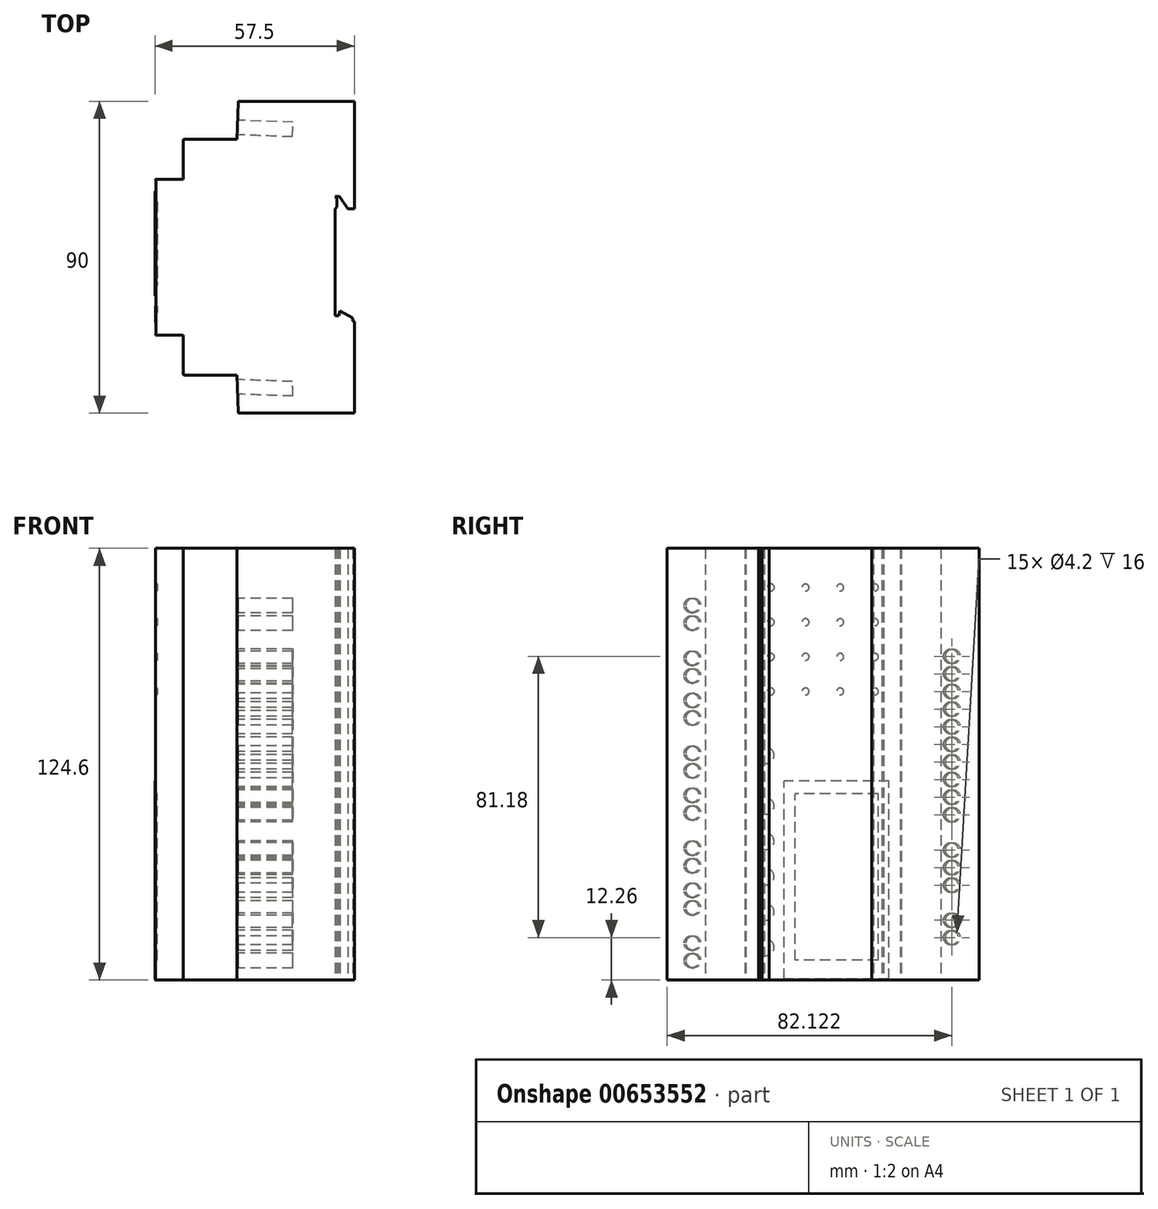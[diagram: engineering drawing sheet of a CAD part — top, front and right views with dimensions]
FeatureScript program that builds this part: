
annotation { "Feature Type Name" : "Feature", "Feature Type Description" : "" }
export const myFeature = defineFeature(function(context is Context, id is Id, definition is map)
    precondition{}
    {
        {
            var Q0;
            Q0=qCreatedBy(makeId("Top.planeOp"),FACE);
            var sketch = newSketch(context, id + "F0", { "sketchPlane" : qUnion([Q0])});
            skLineSegment(sketch, "E0", {"start": v(-15.51, -38) * mm, "end": v(4.7, -38) * mm});
            skLineSegment(sketch, "E1", {"start": v(17.7, -38) * mm, "end": v(17.7, -11.6) * mm});
            skLineSegment(sketch, "E2", {"start": v(5.2, -38) * mm, "end": v(17.7, -38) * mm});
            skLineSegment(sketch, "E3", {"start": v(17.2, -10.59) * mm, "end": v(13.57, -8.5) * mm});
            skLineSegment(sketch, "E4", {"start": v(17.2, -10.59) * mm, "end": v(17.2, -11.46) * mm});
            skLineSegment(sketch, "E5", {"start": v(13.57, -8.5) * mm, "end": v(13.2, -9.9) * mm});
            skLineSegment(sketch, "E6", {"start": v(-31.7, -15.5) * mm, "end": v(-39.4, -15.5) * mm});
            skLineSegment(sketch, "E7", {"start": v(-31.4, -27) * mm, "end": v(-16.19, -27) * mm});
            skLineSegment(sketch, "E8", {"start": v(-16.19, -27) * mm, "end": v(-15.81, -37.7) * mm});
            skArc(sketch, "E9", {"start": v(-15.81, -37.7) * mm, "mid": v(-15.72, -37.9) * mm, "end": v(-15.51, -38) * mm});
            skLineSegment(sketch, "E10", {"start": v(-31.7, -26.7) * mm, "end": v(-31.7, -15.5) * mm});
            skArc(sketch, "E11", {"start": v(-31.7, -26.7) * mm, "mid": v(-31.61, -26.9) * mm, "end": v(-31.4, -27) * mm});
            skLineSegment(sketch, "E12", {"start": v(17.7, 52) * mm, "end": v(-15.51, 52) * mm});
            skLineSegment(sketch, "E13", {"start": v(17.7, 52) * mm, "end": v(17.7, 21) * mm});
            skLineSegment(sketch, "E14", {"start": v(13.4, 24.5) * mm, "end": v(15.85, 21) * mm});
            skLineSegment(sketch, "E15", {"start": v(15.85, 21) * mm, "end": v(17.7, 21) * mm});
            skLineSegment(sketch, "E16", {"start": v(12.7, 24) * mm, "end": v(12.7, 21.5) * mm});
            skLineSegment(sketch, "E17", {"start": v(12.7, 21.5) * mm, "end": v(12.2, 21) * mm});
            skLineSegment(sketch, "E18", {"start": v(12.7, 24) * mm, "end": v(12.2, 24.5) * mm});
            skLineSegment(sketch, "E19", {"start": v(-31.7, 29.5) * mm, "end": v(-39.4, 29.5) * mm});
            skLineSegment(sketch, "E20", {"start": v(-31.7, 29.5) * mm, "end": v(-31.7, 40.7) * mm});
            skLineSegment(sketch, "E21", {"start": v(-16.19, 41) * mm, "end": v(-31.4, 41) * mm});
            skLineSegment(sketch, "E22", {"start": v(-15.81, 51.72) * mm, "end": v(-16.19, 41) * mm});
            skArc(sketch, "E23", {"start": v(-15.51, 52) * mm, "mid": v(-15.72, 51.92) * mm, "end": v(-15.81, 51.72) * mm});
            skArc(sketch, "E24", {"start": v(-31.4, 41) * mm, "mid": v(-31.61, 40.92) * mm, "end": v(-31.7, 40.7) * mm});
            skLineSegment(sketch, "E25", {"start": v(13.2, -9.9) * mm, "end": v(12.2, -9.9) * mm});
            skLineSegment(sketch, "E26", {"start": v(4.7, -38) * mm, "end": v(5.2, -38) * mm});
            skLineSegment(sketch, "E27", {"start": v(13.4, 24.5) * mm, "end": v(12.2, 24.5) * mm});
            skLineSegment(sketch, "E28", {"start": v(12.2, -9.9) * mm, "end": v(12.2, 21) * mm});
            skLineSegment(sketch, "E29", {"start": v(17.2, -11.46) * mm, "end": v(17.7, -11.6) * mm});
            skLineSegment(sketch, "E30", {"start": v(-39.7, 29.2) * mm, "end": v(-39.7, -15.2) * mm});
            skLineSegment(sketch, "E31", {"start": v(-39.7, -15.2) * mm, "end": v(-39.7, -15.5) * mm});
            skLineSegment(sketch, "E32", {"start": v(-39.7, -15.5) * mm, "end": v(-39.4, -15.5) * mm});
            skLineSegment(sketch, "E33", {"start": v(-39.7, 29.2) * mm, "end": v(-39.7, 29.5) * mm});
            skLineSegment(sketch, "E34", {"start": v(-39.7, 29.5) * mm, "end": v(-39.4, 29.5) * mm});
            skSolve(sketch);
        }
        {
            var Q0;
            Q0=makeQuery(id+"F0.imprint","IMPRINT",FACE,{"disambiguationData":[TD([[makeQuery(id+"F0.imprint","IMPRINT",EDGE,{"derivedFrom":sQuery(id+"F0.wireOp",EDGE,"E0")}),1.0]])]});
            extrude(context, id + "F1", {"entities" : qUnion([Q0]), "depth" : 124.6 * mm, "offsetDistance" : 25 * mm});
        }
        {
            var Q0;
            Q0=makeQuery(id+"F1.opExtrude","SWEPT_EDGE",EDGE,{"disambiguationData":[OSD([sQuery(id+"F0.wireOp",EDGE,"E31"),sQuery(id+"F0.wireOp",EDGE,"E32")])]});
            var Q1;
            Q1=makeQuery(id+"F1.opExtrude","SWEPT_EDGE",EDGE,{"disambiguationData":[OSD([sQuery(id+"F0.wireOp",EDGE,"E33"),sQuery(id+"F0.wireOp",EDGE,"E34")])]});
            fillet(context, id + "F2", {"entities" : qUnion([Q0, Q1]), "radius" : 0.25 * mm, "tangentPropagation" : true, "allowEdgeOverflow" : false});
        }
        {
            var Q0;
            Q0=makeQuery(id+"F1.opExtrude","SWEPT_FACE",FACE,{"disambiguationData":[OSD([sQuery(id+"F0.wireOp",EDGE,"E22")])]});
            var sketch = newSketch(context, id + "F3", { "sketchPlane" : qUnion([Q0])});
            skCircle(sketch, "E35", {"center": v(-43.82, 12.26) * mm, "radius": 2.1 * mm});
            skCircle(sketch, "E36", {"center": v(-43.82, 17.26) * mm, "radius": 2.1 * mm});
            skCircle(sketch, "E37", {"center": v(-43.82, 27.4) * mm, "radius": 2.1 * mm});
            skCircle(sketch, "E38.0.1.0", {"center": v(-43.82, 32.48) * mm, "radius": 2.1 * mm});
            skCircle(sketch, "E38.0.2.0", {"center": v(-43.82, 37.56) * mm, "radius": 2.1 * mm});
            skCircle(sketch, "E38.0.3.0", {"center": v(-43.82, 42.64) * mm, "radius": 2.1 * mm});
            skCircle(sketch, "E38.0.4.0", {"center": v(-43.82, 47.72) * mm, "radius": 2.1 * mm});
            skCircle(sketch, "E38.0.5.0", {"center": v(-43.82, 52.8) * mm, "radius": 2.1 * mm});
            skCircle(sketch, "E38.0.6.0", {"center": v(-43.82, 57.88) * mm, "radius": 2.1 * mm});
            skCircle(sketch, "E38.0.7.0", {"center": v(-43.82, 62.96) * mm, "radius": 2.1 * mm});
            skCircle(sketch, "E38.0.8.0", {"center": v(-43.82, 68.04) * mm, "radius": 2.1 * mm});
            skCircle(sketch, "E38.0.9.0", {"center": v(-43.82, 73.12) * mm, "radius": 2.1 * mm});
            skCircle(sketch, "E38.0.10.0", {"center": v(-43.82, 78.2) * mm, "radius": 2.1 * mm});
            skCircle(sketch, "E38.0.11.0", {"center": v(-43.82, 83.28) * mm, "radius": 2.1 * mm});
            skCircle(sketch, "E38.0.12.0", {"center": v(-43.82, 88.36) * mm, "radius": 2.1 * mm});
            skCircle(sketch, "E38.0.13.0", {"center": v(-43.82, 93.44) * mm, "radius": 2.1 * mm});
            skLineSegment(sketch, "E38.direction1", {"start": v(-43.82, 27.4) * mm, "end": v(-18.82, 27.4) * mm, "construction": true});
            skLineSegment(sketch, "E38.direction2", {"start": v(-43.82, 27.4) * mm, "end": v(-43.82, 32.48) * mm, "construction": true});
            skSolve(sketch);
        }
        {
            var Q0;
            Q0=makeQuery(id+"F1.opExtrude","SWEPT_FACE",FACE,{"disambiguationData":[OSD([sQuery(id+"F0.wireOp",EDGE,"E8")])]});
            var sketch = newSketch(context, id + "F4", { "sketchPlane" : qUnion([Q0])});
            skCircle(sketch, "E39", {"center": v(29.83, 5.64) * mm, "radius": 2.1 * mm});
            skCircle(sketch, "E40", {"center": v(29.83, 10.68) * mm, "radius": 2.1 * mm});
            skCircle(sketch, "E41", {"center": v(29.83, 20.84) * mm, "radius": 2.1 * mm});
            skCircle(sketch, "E42", {"center": v(29.83, 25.92) * mm, "radius": 2.1 * mm});
            skCircle(sketch, "E43", {"center": v(29.83, 33) * mm, "radius": 2.1 * mm});
            skCircle(sketch, "E44", {"center": v(29.83, 38.08) * mm, "radius": 2.1 * mm});
            skCircle(sketch, "E45.0.1.0", {"center": v(29.83, 60.4) * mm, "radius": 2.1 * mm});
            skCircle(sketch, "E45.0.1.1", {"center": v(29.83, 65.48) * mm, "radius": 2.1 * mm});
            skCircle(sketch, "E45.0.1.2", {"center": v(29.83, 53.32) * mm, "radius": 2.1 * mm});
            skCircle(sketch, "E45.0.1.3", {"center": v(29.83, 48.24) * mm, "radius": 2.1 * mm});
            skCircle(sketch, "E45.0.2.0", {"center": v(29.83, 87.8) * mm, "radius": 2.1 * mm});
            skCircle(sketch, "E45.0.2.1", {"center": v(29.83, 92.88) * mm, "radius": 2.1 * mm});
            skCircle(sketch, "E45.0.2.2", {"center": v(29.83, 80.72) * mm, "radius": 2.1 * mm});
            skCircle(sketch, "E45.0.2.3", {"center": v(29.83, 75.64) * mm, "radius": 2.1 * mm});
            skLineSegment(sketch, "E45.direction1", {"start": v(29.83, 20.84) * mm, "end": v(54.83, 20.84) * mm, "construction": true});
            skLineSegment(sketch, "E45.direction2", {"start": v(29.83, 20.84) * mm, "end": v(29.83, 48.24) * mm, "construction": true});
            skCircle(sketch, "E46", {"center": v(29.83, 103.04) * mm, "radius": 2.1 * mm});
            skCircle(sketch, "E47", {"center": v(29.83, 108.12) * mm, "radius": 2.1 * mm});
            skSolve(sketch);
        }
        {
            var Q0;
            Q0=makeQuery(id+"F1.opExtrude","SWEPT_FACE",FACE,{"disambiguationData":[OSD([sQuery(id+"F0.wireOp",EDGE,"E30"),sQuery(id+"F0.wireOp",EDGE,"E31"),sQuery(id+"F0.wireOp",EDGE,"E33")])]});
            var sketch = newSketch(context, id + "F5", { "sketchPlane" : qUnion([Q0])});
            skLineSegment(sketch, "E48.bottom", {"start": v(-22.9, 5.8) * mm, "end": v(1.1, 5.8) * mm});
            skLineSegment(sketch, "E48.top", {"start": v(-22.9, 53.8) * mm, "end": v(1.1, 53.8) * mm});
            skLineSegment(sketch, "E48.left", {"start": v(-22.9, 5.8) * mm, "end": v(-22.9, 53.8) * mm});
            skLineSegment(sketch, "E48.right", {"start": v(1.1, 5.8) * mm, "end": v(1.1, 53.8) * mm});
            skCircle(sketch, "E49", {"center": v(9.5, 9.42) * mm, "radius": 3.57 * mm});
            skCircle(sketch, "E50", {"center": v(9.5, 9.42) * mm, "radius": 2.35 * mm});
            skCircle(sketch, "E51.0.1.0", {"center": v(9.5, 19.62) * mm, "radius": 3.57 * mm});
            skCircle(sketch, "E51.0.1.1", {"center": v(9.5, 19.62) * mm, "radius": 2.35 * mm});
            skCircle(sketch, "E51.0.2.0", {"center": v(9.5, 29.82) * mm, "radius": 3.57 * mm});
            skCircle(sketch, "E51.0.2.1", {"center": v(9.5, 29.82) * mm, "radius": 2.35 * mm});
            skCircle(sketch, "E51.0.3.0", {"center": v(9.5, 40.02) * mm, "radius": 3.57 * mm});
            skCircle(sketch, "E51.0.3.1", {"center": v(9.5, 40.02) * mm, "radius": 2.35 * mm});
            skCircle(sketch, "E51.0.4.0", {"center": v(9.5, 50.22) * mm, "radius": 3.57 * mm});
            skCircle(sketch, "E51.0.4.1", {"center": v(9.5, 50.22) * mm, "radius": 2.35 * mm});
            skLineSegment(sketch, "E51.direction1", {"start": v(9.5, 9.42) * mm, "end": v(34.5, 9.42) * mm, "construction": true});
            skLineSegment(sketch, "E51.direction2", {"start": v(9.5, 9.42) * mm, "end": v(9.5, 19.62) * mm, "construction": true});
            skCircle(sketch, "E52.0.1.0", {"center": v(9.5, 64.82) * mm, "radius": 2.35 * mm});
            skCircle(sketch, "E52.0.1.1", {"center": v(9.5, 64.82) * mm, "radius": 3.57 * mm});
            skLineSegment(sketch, "E52.direction1", {"start": v(9.5, 50.22) * mm, "end": v(34.5, 50.22) * mm, "construction": true});
            skLineSegment(sketch, "E52.direction2", {"start": v(9.5, 50.22) * mm, "end": v(9.5, 64.82) * mm, "construction": true});
            skLineSegment(sketch, "E53.bottom", {"start": v(-26.06, 0.3) * mm, "end": v(4.24, 0.3) * mm});
            skLineSegment(sketch, "E53.top", {"start": v(-26.06, 57.4) * mm, "end": v(4.24, 57.4) * mm});
            skLineSegment(sketch, "E53.left", {"start": v(-26.06, 0.3) * mm, "end": v(-26.06, 57.4) * mm});
            skLineSegment(sketch, "E53.right", {"start": v(4.24, 0.3) * mm, "end": v(4.24, 57.4) * mm});
            skCircle(sketch, "E54", {"center": v(-21.95, 113.3) * mm, "radius": 1 * mm});
            skCircle(sketch, "E55.0.1.0", {"center": v(-21.95, 103.3) * mm, "radius": 1 * mm});
            skCircle(sketch, "E55.0.2.0", {"center": v(-21.95, 93.3) * mm, "radius": 1 * mm});
            skCircle(sketch, "E55.0.3.0", {"center": v(-21.95, 83.3) * mm, "radius": 1 * mm});
            skCircle(sketch, "E55.1.0.0", {"center": v(-11.95, 113.3) * mm, "radius": 1 * mm});
            skCircle(sketch, "E55.1.1.0", {"center": v(-11.95, 103.3) * mm, "radius": 1 * mm});
            skCircle(sketch, "E55.1.2.0", {"center": v(-11.95, 93.3) * mm, "radius": 1 * mm});
            skCircle(sketch, "E55.1.3.0", {"center": v(-11.95, 83.3) * mm, "radius": 1 * mm});
            skCircle(sketch, "E55.2.0.0", {"center": v(-1.95, 113.3) * mm, "radius": 1 * mm});
            skCircle(sketch, "E55.2.1.0", {"center": v(-1.95, 103.3) * mm, "radius": 1 * mm});
            skCircle(sketch, "E55.2.2.0", {"center": v(-1.95, 93.3) * mm, "radius": 1 * mm});
            skCircle(sketch, "E55.2.3.0", {"center": v(-1.95, 83.3) * mm, "radius": 1 * mm});
            skCircle(sketch, "E55.3.0.0", {"center": v(8.05, 113.3) * mm, "radius": 1 * mm});
            skCircle(sketch, "E55.3.1.0", {"center": v(8.05, 103.3) * mm, "radius": 1 * mm});
            skCircle(sketch, "E55.3.2.0", {"center": v(8.05, 93.3) * mm, "radius": 1 * mm});
            skCircle(sketch, "E55.3.3.0", {"center": v(8.05, 83.3) * mm, "radius": 1 * mm});
            skLineSegment(sketch, "E55.direction1", {"start": v(-21.95, 113.3) * mm, "end": v(-11.95, 113.3) * mm, "construction": true});
            skLineSegment(sketch, "E55.direction2", {"start": v(-21.95, 113.3) * mm, "end": v(-21.95, 103.3) * mm, "construction": true});
            skSolve(sketch);
        }
        {
            var Q0;
            Q0=makeQuery(id+"F3.imprint","IMPRINT",FACE,{"disambiguationData":[TD([[makeQuery(id+"F3.imprint","IMPRINT",EDGE,{"derivedFrom":sQuery(id+"F3.wireOp",EDGE,"E36")}),1.0]])]});
            var Q1;
            Q1=makeQuery(id+"F3.imprint","IMPRINT",FACE,{"disambiguationData":[TD([[makeQuery(id+"F3.imprint","IMPRINT",EDGE,{"derivedFrom":sQuery(id+"F3.wireOp",EDGE,"E35")}),1.0]])]});
            var Q2;
            Q2=makeQuery(id+"F3.imprint","IMPRINT",FACE,{"disambiguationData":[TD([[makeQuery(id+"F3.imprint","IMPRINT",EDGE,{"derivedFrom":sQuery(id+"F3.wireOp",EDGE,"E37")}),1.0]])]});
            var Q3;
            Q3=makeQuery(id+"F3.imprint","IMPRINT",FACE,{"disambiguationData":[TD([[makeQuery(id+"F3.imprint","IMPRINT",EDGE,{"derivedFrom":sQuery(id+"F3.wireOp",EDGE,"E38.0.1.0")}),1.0]])]});
            var Q4;
            Q4=makeQuery(id+"F3.imprint","IMPRINT",FACE,{"disambiguationData":[TD([[makeQuery(id+"F3.imprint","IMPRINT",EDGE,{"derivedFrom":sQuery(id+"F3.wireOp",EDGE,"E38.0.2.0")}),1.0]])]});
            var Q5;
            Q5=makeQuery(id+"F3.imprint","IMPRINT",FACE,{"disambiguationData":[TD([[makeQuery(id+"F3.imprint","IMPRINT",EDGE,{"derivedFrom":sQuery(id+"F3.wireOp",EDGE,"E38.0.4.0")}),1.0]])]});
            var Q6;
            Q6=makeQuery(id+"F3.imprint","IMPRINT",FACE,{"disambiguationData":[TD([[makeQuery(id+"F3.imprint","IMPRINT",EDGE,{"derivedFrom":sQuery(id+"F3.wireOp",EDGE,"E38.0.5.0")}),1.0]])]});
            var Q7;
            Q7=makeQuery(id+"F3.imprint","IMPRINT",FACE,{"disambiguationData":[TD([[makeQuery(id+"F3.imprint","IMPRINT",EDGE,{"derivedFrom":sQuery(id+"F3.wireOp",EDGE,"E38.0.6.0")}),1.0]])]});
            var Q8;
            Q8=makeQuery(id+"F3.imprint","IMPRINT",FACE,{"disambiguationData":[TD([[makeQuery(id+"F3.imprint","IMPRINT",EDGE,{"derivedFrom":sQuery(id+"F3.wireOp",EDGE,"E38.0.7.0")}),1.0]])]});
            var Q9;
            Q9=makeQuery(id+"F3.imprint","IMPRINT",FACE,{"disambiguationData":[TD([[makeQuery(id+"F3.imprint","IMPRINT",EDGE,{"derivedFrom":sQuery(id+"F3.wireOp",EDGE,"E38.0.8.0")}),1.0]])]});
            var Q10;
            Q10=makeQuery(id+"F3.imprint","IMPRINT",FACE,{"disambiguationData":[TD([[makeQuery(id+"F3.imprint","IMPRINT",EDGE,{"derivedFrom":sQuery(id+"F3.wireOp",EDGE,"E38.0.9.0")}),1.0]])]});
            var Q11;
            Q11=makeQuery(id+"F3.imprint","IMPRINT",FACE,{"disambiguationData":[TD([[makeQuery(id+"F3.imprint","IMPRINT",EDGE,{"derivedFrom":sQuery(id+"F3.wireOp",EDGE,"E38.0.10.0")}),1.0]])]});
            var Q12;
            Q12=makeQuery(id+"F3.imprint","IMPRINT",FACE,{"disambiguationData":[TD([[makeQuery(id+"F3.imprint","IMPRINT",EDGE,{"derivedFrom":sQuery(id+"F3.wireOp",EDGE,"E38.0.11.0")}),1.0]])]});
            var Q13;
            Q13=makeQuery(id+"F3.imprint","IMPRINT",FACE,{"disambiguationData":[TD([[makeQuery(id+"F3.imprint","IMPRINT",EDGE,{"derivedFrom":sQuery(id+"F3.wireOp",EDGE,"E38.0.12.0")}),1.0]])]});
            var Q14;
            Q14=makeQuery(id+"F3.imprint","IMPRINT",FACE,{"disambiguationData":[TD([[makeQuery(id+"F3.imprint","IMPRINT",EDGE,{"derivedFrom":sQuery(id+"F3.wireOp",EDGE,"E38.0.13.0")}),1.0]])]});
            var Q15;
            Q15=makeQuery(id+"F4.imprint","IMPRINT",FACE,{"disambiguationData":[TD([[makeQuery(id+"F4.imprint","IMPRINT",EDGE,{"derivedFrom":sQuery(id+"F4.wireOp",EDGE,"E39")}),1.0]])]});
            var Q16;
            Q16=makeQuery(id+"F4.imprint","IMPRINT",FACE,{"disambiguationData":[TD([[makeQuery(id+"F4.imprint","IMPRINT",EDGE,{"derivedFrom":sQuery(id+"F4.wireOp",EDGE,"E40")}),1.0]])]});
            var Q17;
            Q17=makeQuery(id+"F4.imprint","IMPRINT",FACE,{"disambiguationData":[TD([[makeQuery(id+"F4.imprint","IMPRINT",EDGE,{"derivedFrom":sQuery(id+"F4.wireOp",EDGE,"E41")}),1.0]])]});
            var Q18;
            Q18=makeQuery(id+"F4.imprint","IMPRINT",FACE,{"disambiguationData":[TD([[makeQuery(id+"F4.imprint","IMPRINT",EDGE,{"derivedFrom":sQuery(id+"F4.wireOp",EDGE,"E42")}),1.0]])]});
            var Q19;
            Q19=makeQuery(id+"F4.imprint","IMPRINT",FACE,{"disambiguationData":[TD([[makeQuery(id+"F4.imprint","IMPRINT",EDGE,{"derivedFrom":sQuery(id+"F4.wireOp",EDGE,"E43")}),1.0]])]});
            var Q20;
            Q20=makeQuery(id+"F4.imprint","IMPRINT",FACE,{"disambiguationData":[TD([[makeQuery(id+"F4.imprint","IMPRINT",EDGE,{"derivedFrom":sQuery(id+"F4.wireOp",EDGE,"E44")}),1.0]])]});
            var Q21;
            Q21=makeQuery(id+"F4.imprint","IMPRINT",FACE,{"disambiguationData":[TD([[makeQuery(id+"F4.imprint","IMPRINT",EDGE,{"derivedFrom":sQuery(id+"F4.wireOp",EDGE,"E45.0.1.3")}),1.0]])]});
            var Q22;
            Q22=makeQuery(id+"F4.imprint","IMPRINT",FACE,{"disambiguationData":[TD([[makeQuery(id+"F4.imprint","IMPRINT",EDGE,{"derivedFrom":sQuery(id+"F4.wireOp",EDGE,"E45.0.1.2")}),1.0]])]});
            var Q23;
            Q23=makeQuery(id+"F4.imprint","IMPRINT",FACE,{"disambiguationData":[TD([[makeQuery(id+"F4.imprint","IMPRINT",EDGE,{"derivedFrom":sQuery(id+"F4.wireOp",EDGE,"E45.0.1.0")}),1.0]])]});
            var Q24;
            Q24=makeQuery(id+"F4.imprint","IMPRINT",FACE,{"disambiguationData":[TD([[makeQuery(id+"F4.imprint","IMPRINT",EDGE,{"derivedFrom":sQuery(id+"F4.wireOp",EDGE,"E45.0.1.1")}),1.0]])]});
            var Q25;
            Q25=makeQuery(id+"F4.imprint","IMPRINT",FACE,{"disambiguationData":[TD([[makeQuery(id+"F4.imprint","IMPRINT",EDGE,{"derivedFrom":sQuery(id+"F4.wireOp",EDGE,"E45.0.2.3")}),1.0]])]});
            var Q26;
            Q26=makeQuery(id+"F4.imprint","IMPRINT",FACE,{"disambiguationData":[TD([[makeQuery(id+"F4.imprint","IMPRINT",EDGE,{"derivedFrom":sQuery(id+"F4.wireOp",EDGE,"E45.0.2.2")}),1.0]])]});
            var Q27;
            Q27=makeQuery(id+"F4.imprint","IMPRINT",FACE,{"disambiguationData":[TD([[makeQuery(id+"F4.imprint","IMPRINT",EDGE,{"derivedFrom":sQuery(id+"F4.wireOp",EDGE,"E45.0.2.0")}),1.0]])]});
            var Q28;
            Q28=makeQuery(id+"F4.imprint","IMPRINT",FACE,{"disambiguationData":[TD([[makeQuery(id+"F4.imprint","IMPRINT",EDGE,{"derivedFrom":sQuery(id+"F4.wireOp",EDGE,"E45.0.2.1")}),1.0]])]});
            var Q29;
            Q29=makeQuery(id+"F4.imprint","IMPRINT",FACE,{"disambiguationData":[TD([[makeQuery(id+"F4.imprint","IMPRINT",EDGE,{"derivedFrom":sQuery(id+"F4.wireOp",EDGE,"E46")}),1.0]])]});
            var Q30;
            Q30=makeQuery(id+"F4.imprint","IMPRINT",FACE,{"disambiguationData":[TD([[makeQuery(id+"F4.imprint","IMPRINT",EDGE,{"derivedFrom":sQuery(id+"F4.wireOp",EDGE,"E47")}),1.0]])]});
            extrude(context, id + "F6", {"entities" : qUnion([Q0, Q1, Q2, Q3, Q4, Q5, Q6, Q7, Q8, Q9, Q10, Q11, Q12, Q13, Q14, Q15, Q16, Q17, Q18, Q19, Q20, Q21, Q22, Q23, Q24, Q25, Q26, Q27, Q28, Q29, Q30]), "operationType" : NewBodyOperationType.REMOVE, "oppositeDirection" : true, "depth" : 16 * mm, "offsetDistance" : 25 * mm});
        }
        {
            var Q0;
            Q0=makeQuery(id+"F5.imprint","IMPRINT",FACE,{"disambiguationData":[TD([[makeQuery(id+"F5.imprint","IMPRINT",EDGE,{"derivedFrom":sQuery(id+"F5.wireOp",EDGE,"E49")}),-1.0]])]});
            var Q1;
            Q1=makeQuery(id+"F5.imprint","IMPRINT",FACE,{"disambiguationData":[TD([[makeQuery(id+"F5.imprint","IMPRINT",EDGE,{"derivedFrom":sQuery(id+"F5.wireOp",EDGE,"E49")}),1.0]])]});
            var Q2;
            Q2=makeQuery(id+"F5.imprint","IMPRINT",FACE,{"disambiguationData":[TD([[makeQuery(id+"F5.imprint","IMPRINT",EDGE,{"derivedFrom":sQuery(id+"F5.wireOp",EDGE,"E51.0.1.0")}),1.0]])]});
            var Q3;
            Q3=makeQuery(id+"F5.imprint","IMPRINT",FACE,{"disambiguationData":[TD([[makeQuery(id+"F5.imprint","IMPRINT",EDGE,{"derivedFrom":sQuery(id+"F5.wireOp",EDGE,"E51.0.2.0")}),1.0]])]});
            var Q4;
            Q4=makeQuery(id+"F5.imprint","IMPRINT",FACE,{"disambiguationData":[TD([[makeQuery(id+"F5.imprint","IMPRINT",EDGE,{"derivedFrom":sQuery(id+"F5.wireOp",EDGE,"E51.0.3.0")}),1.0]])]});
            var Q5;
            Q5=makeQuery(id+"F5.imprint","IMPRINT",FACE,{"disambiguationData":[TD([[makeQuery(id+"F5.imprint","IMPRINT",EDGE,{"derivedFrom":sQuery(id+"F5.wireOp",EDGE,"E51.0.4.0")}),1.0]])]});
            var Q6;
            Q6=makeQuery(id+"F5.imprint","IMPRINT",FACE,{"disambiguationData":[TD([[makeQuery(id+"F5.imprint","IMPRINT",EDGE,{"derivedFrom":sQuery(id+"F5.wireOp",EDGE,"E55.0.3.0")}),1.0]])]});
            var Q7;
            Q7=makeQuery(id+"F5.imprint","IMPRINT",FACE,{"disambiguationData":[TD([[makeQuery(id+"F5.imprint","IMPRINT",EDGE,{"derivedFrom":sQuery(id+"F5.wireOp",EDGE,"E55.0.2.0")}),1.0]])]});
            var Q8;
            Q8=makeQuery(id+"F5.imprint","IMPRINT",FACE,{"disambiguationData":[TD([[makeQuery(id+"F5.imprint","IMPRINT",EDGE,{"derivedFrom":sQuery(id+"F5.wireOp",EDGE,"E55.0.1.0")}),1.0]])]});
            var Q9;
            Q9=makeQuery(id+"F5.imprint","IMPRINT",FACE,{"disambiguationData":[TD([[makeQuery(id+"F5.imprint","IMPRINT",EDGE,{"derivedFrom":sQuery(id+"F5.wireOp",EDGE,"E54")}),1.0]])]});
            var Q10;
            Q10=makeQuery(id+"F5.imprint","IMPRINT",FACE,{"disambiguationData":[TD([[makeQuery(id+"F5.imprint","IMPRINT",EDGE,{"derivedFrom":sQuery(id+"F5.wireOp",EDGE,"E55.1.0.0")}),1.0]])]});
            var Q11;
            Q11=makeQuery(id+"F5.imprint","IMPRINT",FACE,{"disambiguationData":[TD([[makeQuery(id+"F5.imprint","IMPRINT",EDGE,{"derivedFrom":sQuery(id+"F5.wireOp",EDGE,"E55.1.1.0")}),1.0]])]});
            var Q12;
            Q12=makeQuery(id+"F5.imprint","IMPRINT",FACE,{"disambiguationData":[TD([[makeQuery(id+"F5.imprint","IMPRINT",EDGE,{"derivedFrom":sQuery(id+"F5.wireOp",EDGE,"E55.1.2.0")}),1.0]])]});
            var Q13;
            Q13=makeQuery(id+"F5.imprint","IMPRINT",FACE,{"disambiguationData":[TD([[makeQuery(id+"F5.imprint","IMPRINT",EDGE,{"derivedFrom":sQuery(id+"F5.wireOp",EDGE,"E55.1.3.0")}),1.0]])]});
            var Q14;
            Q14=makeQuery(id+"F5.imprint","IMPRINT",FACE,{"disambiguationData":[TD([[makeQuery(id+"F5.imprint","IMPRINT",EDGE,{"derivedFrom":sQuery(id+"F5.wireOp",EDGE,"E55.2.3.0")}),1.0]])]});
            var Q15;
            Q15=makeQuery(id+"F5.imprint","IMPRINT",FACE,{"disambiguationData":[TD([[makeQuery(id+"F5.imprint","IMPRINT",EDGE,{"derivedFrom":sQuery(id+"F5.wireOp",EDGE,"E55.2.2.0")}),1.0]])]});
            var Q16;
            Q16=makeQuery(id+"F5.imprint","IMPRINT",FACE,{"disambiguationData":[TD([[makeQuery(id+"F5.imprint","IMPRINT",EDGE,{"derivedFrom":sQuery(id+"F5.wireOp",EDGE,"E55.2.1.0")}),1.0]])]});
            var Q17;
            Q17=makeQuery(id+"F5.imprint","IMPRINT",FACE,{"disambiguationData":[TD([[makeQuery(id+"F5.imprint","IMPRINT",EDGE,{"derivedFrom":sQuery(id+"F5.wireOp",EDGE,"E55.2.0.0")}),1.0]])]});
            var Q18;
            Q18=makeQuery(id+"F5.imprint","IMPRINT",FACE,{"disambiguationData":[TD([[makeQuery(id+"F5.imprint","IMPRINT",EDGE,{"derivedFrom":sQuery(id+"F5.wireOp",EDGE,"E55.3.0.0")}),1.0]])]});
            var Q19;
            Q19=makeQuery(id+"F5.imprint","IMPRINT",FACE,{"disambiguationData":[TD([[makeQuery(id+"F5.imprint","IMPRINT",EDGE,{"derivedFrom":sQuery(id+"F5.wireOp",EDGE,"E55.3.1.0")}),1.0]])]});
            var Q20;
            Q20=makeQuery(id+"F5.imprint","IMPRINT",FACE,{"disambiguationData":[TD([[makeQuery(id+"F5.imprint","IMPRINT",EDGE,{"derivedFrom":sQuery(id+"F5.wireOp",EDGE,"E55.3.2.0")}),1.0]])]});
            var Q21;
            Q21=makeQuery(id+"F5.imprint","IMPRINT",FACE,{"disambiguationData":[TD([[makeQuery(id+"F5.imprint","IMPRINT",EDGE,{"derivedFrom":sQuery(id+"F5.wireOp",EDGE,"E55.3.3.0")}),1.0]])]});
            var Q22;
            Q22=makeQuery(id+"F5.imprint","IMPRINT",FACE,{"disambiguationData":[TD([[makeQuery(id+"F5.imprint","IMPRINT",EDGE,{"derivedFrom":sQuery(id+"F5.wireOp",EDGE,"E52.0.1.0")}),-1.0]])]});
            var Q23;
            Q23=makeQuery(id+"F5.imprint","IMPRINT",FACE,{"disambiguationData":[TD([[makeQuery(id+"F5.imprint","IMPRINT",EDGE,{"derivedFrom":sQuery(id+"F5.wireOp",EDGE,"E48.bottom")}),1.0]])]});
            var Q24;
            Q24=makeQuery(id+"F5.imprint","IMPRINT",FACE,{"disambiguationData":[TD([[makeQuery(id+"F5.imprint","IMPRINT",EDGE,{"derivedFrom":sQuery(id+"F5.wireOp",EDGE,"E48.bottom")}),-1.0]])]});
            extrude(context, id + "F7", {"entities" : qUnion([Q0, Q1, Q2, Q3, Q4, Q5, Q6, Q7, Q8, Q9, Q10, Q11, Q12, Q13, Q14, Q15, Q16, Q17, Q18, Q19, Q20, Q21, Q22, Q23, Q24]), "operationType" : NewBodyOperationType.REMOVE, "oppositeDirection" : true, "depth" : 0.2 * mm, "offsetDistance" : 25 * mm});
        }
        {
            var Q0;
            Q0=makeQuery(id+"F5.imprint","IMPRINT",FACE,{"disambiguationData":[TD([[makeQuery(id+"F5.imprint","IMPRINT",EDGE,{"derivedFrom":sQuery(id+"F5.wireOp",EDGE,"E48.bottom")}),1.0]])]});
            var Q1;
            Q1=makeQuery(id+"F5.imprint","IMPRINT",FACE,{"disambiguationData":[TD([[makeQuery(id+"F5.imprint","IMPRINT",EDGE,{"derivedFrom":sQuery(id+"F5.wireOp",EDGE,"E55.0.3.0")}),1.0]])]});
            var Q2;
            Q2=makeQuery(id+"F5.imprint","IMPRINT",FACE,{"disambiguationData":[TD([[makeQuery(id+"F5.imprint","IMPRINT",EDGE,{"derivedFrom":sQuery(id+"F5.wireOp",EDGE,"E55.0.2.0")}),1.0]])]});
            var Q3;
            Q3=makeQuery(id+"F5.imprint","IMPRINT",FACE,{"disambiguationData":[TD([[makeQuery(id+"F5.imprint","IMPRINT",EDGE,{"derivedFrom":sQuery(id+"F5.wireOp",EDGE,"E55.0.1.0")}),1.0]])]});
            var Q4;
            Q4=makeQuery(id+"F5.imprint","IMPRINT",FACE,{"disambiguationData":[TD([[makeQuery(id+"F5.imprint","IMPRINT",EDGE,{"derivedFrom":sQuery(id+"F5.wireOp",EDGE,"E55.1.3.0")}),1.0]])]});
            var Q5;
            Q5=makeQuery(id+"F5.imprint","IMPRINT",FACE,{"disambiguationData":[TD([[makeQuery(id+"F5.imprint","IMPRINT",EDGE,{"derivedFrom":sQuery(id+"F5.wireOp",EDGE,"E55.1.2.0")}),1.0]])]});
            var Q6;
            Q6=makeQuery(id+"F5.imprint","IMPRINT",FACE,{"disambiguationData":[TD([[makeQuery(id+"F5.imprint","IMPRINT",EDGE,{"derivedFrom":sQuery(id+"F5.wireOp",EDGE,"E55.1.1.0")}),1.0]])]});
            var Q7;
            Q7=makeQuery(id+"F5.imprint","IMPRINT",FACE,{"disambiguationData":[TD([[makeQuery(id+"F5.imprint","IMPRINT",EDGE,{"derivedFrom":sQuery(id+"F5.wireOp",EDGE,"E55.2.3.0")}),1.0]])]});
            var Q8;
            Q8=makeQuery(id+"F5.imprint","IMPRINT",FACE,{"disambiguationData":[TD([[makeQuery(id+"F5.imprint","IMPRINT",EDGE,{"derivedFrom":sQuery(id+"F5.wireOp",EDGE,"E55.2.2.0")}),1.0]])]});
            var Q9;
            Q9=makeQuery(id+"F5.imprint","IMPRINT",FACE,{"disambiguationData":[TD([[makeQuery(id+"F5.imprint","IMPRINT",EDGE,{"derivedFrom":sQuery(id+"F5.wireOp",EDGE,"E55.3.3.0")}),1.0]])]});
            var Q10;
            Q10=makeQuery(id+"F5.imprint","IMPRINT",FACE,{"disambiguationData":[TD([[makeQuery(id+"F5.imprint","IMPRINT",EDGE,{"derivedFrom":sQuery(id+"F5.wireOp",EDGE,"E55.3.2.0")}),1.0]])]});
            var Q11;
            Q11=makeQuery(id+"F5.imprint","IMPRINT",FACE,{"disambiguationData":[TD([[makeQuery(id+"F5.imprint","IMPRINT",EDGE,{"derivedFrom":sQuery(id+"F5.wireOp",EDGE,"E55.2.1.0")}),1.0]])]});
            var Q12;
            Q12=makeQuery(id+"F5.imprint","IMPRINT",FACE,{"disambiguationData":[TD([[makeQuery(id+"F5.imprint","IMPRINT",EDGE,{"derivedFrom":sQuery(id+"F5.wireOp",EDGE,"E55.3.1.0")}),1.0]])]});
            var Q13;
            Q13=makeQuery(id+"F5.imprint","IMPRINT",FACE,{"disambiguationData":[TD([[makeQuery(id+"F5.imprint","IMPRINT",EDGE,{"derivedFrom":sQuery(id+"F5.wireOp",EDGE,"E55.3.0.0")}),1.0]])]});
            var Q14;
            Q14=makeQuery(id+"F5.imprint","IMPRINT",FACE,{"disambiguationData":[TD([[makeQuery(id+"F5.imprint","IMPRINT",EDGE,{"derivedFrom":sQuery(id+"F5.wireOp",EDGE,"E55.2.0.0")}),1.0]])]});
            var Q15;
            Q15=makeQuery(id+"F5.imprint","IMPRINT",FACE,{"disambiguationData":[TD([[makeQuery(id+"F5.imprint","IMPRINT",EDGE,{"derivedFrom":sQuery(id+"F5.wireOp",EDGE,"E55.1.0.0")}),1.0]])]});
            var Q16;
            Q16=makeQuery(id+"F5.imprint","IMPRINT",FACE,{"disambiguationData":[TD([[makeQuery(id+"F5.imprint","IMPRINT",EDGE,{"derivedFrom":sQuery(id+"F5.wireOp",EDGE,"E54")}),1.0]])]});
            extrude(context, id + "F8", {"entities" : qUnion([Q0, Q1, Q2, Q3, Q4, Q5, Q6, Q7, Q8, Q9, Q10, Q11, Q12, Q13, Q14, Q15, Q16]), "operationType" : NewBodyOperationType.REMOVE, "oppositeDirection" : true, "depth" : .5 * mm, "offsetDistance" : 25 * mm});
        }
        {
            var Q0;
            Q0=makeQuery(id+"F5.imprint","IMPRINT",FACE,{"disambiguationData":[TD([[makeQuery(id+"F5.imprint","IMPRINT",EDGE,{"derivedFrom":sQuery(id+"F5.wireOp",EDGE,"E48.bottom")}),-1.0]])]});
            extrude(context, id + "F9", {"entities" : qUnion([Q0]), "depth" : 0.1 * mm, "offsetDistance" : 25 * mm});
        }
        {
            var Q0;
            {var subQ0=sQuery(id+"F0.wireOp",EDGE,"E33");var subQ1=sQuery(id+"F0.wireOp",EDGE,"E32");var subQ2=sQuery(id+"F0.wireOp",EDGE,"E31");var subQ3=sQuery(id+"F0.wireOp",EDGE,"E30");Q0=makeQuery(id+"F7.boolean.opBoolean","MERGE",EDGE,{"derivedFrom":[makeQuery(id+"F2.opFillet","BLEND_EDGE",EDGE,{"blendedFrom":[makeQuery(id+"F1.opExtrude","SWEPT_EDGE",EDGE,{"disambiguationData":[OSD([subQ2,subQ1])]}),makeQuery(id+"F1.opExtrude","SWEPT_FACE",FACE,{"disambiguationData":[OSD([subQ3,subQ2,subQ0])]})],"blendedInto":[makeQuery(id+"F1.opExtrude","SWEPT_FACE",FACE,{"disambiguationData":[OSD([subQ3,subQ2,subQ0])]})]}),makeQuery(id+"F7.opExtrude","CAP_EDGE",EDGE,{"disambiguationData":[OSD([subQ3,subQ2,subQ1,subQ0])],"isStart":true})]});}
            var Q1;
            {var subQ0=sQuery(id+"F0.wireOp",EDGE,"E34");var subQ1=sQuery(id+"F0.wireOp",EDGE,"E33");var subQ2=sQuery(id+"F0.wireOp",EDGE,"E31");var subQ3=sQuery(id+"F0.wireOp",EDGE,"E30");Q1=makeQuery(id+"F7.boolean.opBoolean","MERGE",EDGE,{"derivedFrom":[makeQuery(id+"F2.opFillet","BLEND_EDGE",EDGE,{"blendedFrom":[makeQuery(id+"F1.opExtrude","SWEPT_EDGE",EDGE,{"disambiguationData":[OSD([subQ1,subQ0])]}),makeQuery(id+"F1.opExtrude","SWEPT_FACE",FACE,{"disambiguationData":[OSD([subQ3,subQ2,subQ1])]})],"blendedInto":[makeQuery(id+"F1.opExtrude","SWEPT_FACE",FACE,{"disambiguationData":[OSD([subQ3,subQ2,subQ1])]})]}),makeQuery(id+"F7.opExtrude","CAP_EDGE",EDGE,{"disambiguationData":[OSD([subQ3,subQ2,subQ1,subQ0])],"isStart":true})]});}
            fillet(context, id + "F10", {"entities" : qUnion([Q0, Q1]), "radius" : 0.1 * mm, "tangentPropagation" : true, "allowEdgeOverflow" : false});
        }
    });
